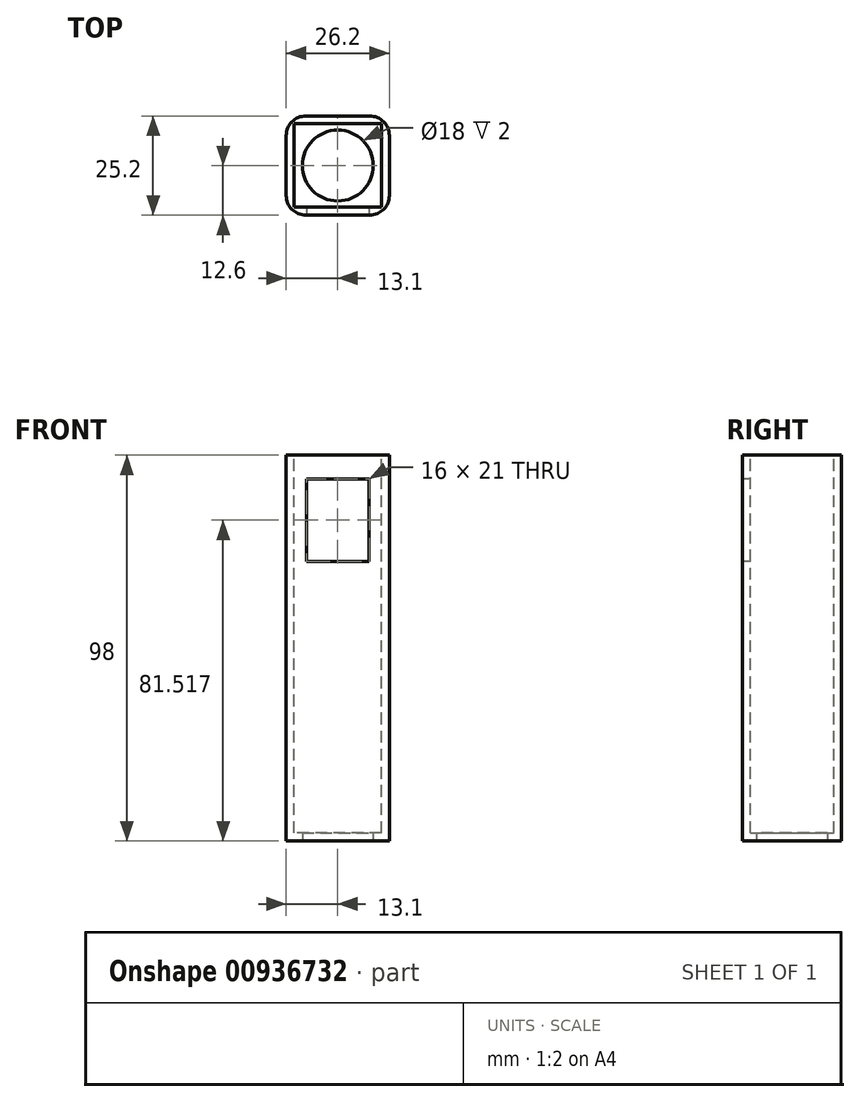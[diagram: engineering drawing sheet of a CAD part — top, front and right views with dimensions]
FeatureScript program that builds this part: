
annotation { "Feature Type Name" : "Feature", "Feature Type Description" : "" }
export const myFeature = defineFeature(function(context is Context, id is Id, definition is map)
    precondition{}
    {
        {
            var Q0;
            Q0=qCreatedBy(makeId("Top.planeOp"),FACE);
            var sketch = newSketch(context, id + "F0", { "sketchPlane" : qUnion([Q0])});
            skLineSegment(sketch, "E0.bottom", {"start": v(13.1, -12.6) * mm, "end": v(-13.1, -12.6) * mm});
            skLineSegment(sketch, "E0.top", {"start": v(13.1, 12.6) * mm, "end": v(-13.1, 12.6) * mm});
            skLineSegment(sketch, "E0.left", {"start": v(13.1, -12.6) * mm, "end": v(13.1, 12.6) * mm});
            skLineSegment(sketch, "E0.right", {"start": v(-13.1, -12.6) * mm, "end": v(-13.1, 12.6) * mm});
            skPoint(sketch, "E0.middle", {"position": v(0, 0) * mm});
            skSolve(sketch);
        }
        {
            var Q0;
            Q0=makeQuery(id+"F0.imprint","IMPRINT",FACE,{"disambiguationData":[TD([[makeQuery(id+"F0.imprint","IMPRINT",EDGE,{"derivedFrom":sQuery(id+"F0.wireOp",EDGE,"E0.bottom")}),-1.0]])]});
            extrude(context, id + "F1", {"entities" : qUnion([Q0]), "oppositeDirection" : true, "depth" : 98 * mm, "offsetDistance" : 25 * mm});
        }
        {
            var Q0;
            Q0=makeQuery(id+"F1.opExtrude","CAP_FACE",FACE,{"disambiguationData":[OSD([sQuery(id+"F0.wireOp",EDGE,"E0.bottom"),sQuery(id+"F0.wireOp",EDGE,"E0.top"),sQuery(id+"F0.wireOp",EDGE,"E0.left"),sQuery(id+"F0.wireOp",EDGE,"E0.right")])],"isStart":true});
            shell(context, id + "F2", {"entities" : qUnion([Q0]), "thickness" : 2 * mm});
        }
        {
            var Q0;
            Q0=makeQuery(id+"F1.opExtrude","CAP_FACE",FACE,{"disambiguationData":[OSD([sQuery(id+"F0.wireOp",EDGE,"E0.bottom"),sQuery(id+"F0.wireOp",EDGE,"E0.top"),sQuery(id+"F0.wireOp",EDGE,"E0.left"),sQuery(id+"F0.wireOp",EDGE,"E0.right")])],"isStart":false});
            var sketch = newSketch(context, id + "F3", { "sketchPlane" : qUnion([Q0])});
            skCircle(sketch, "E1", {"center": v(0, 0) * mm, "radius": 9 * mm});
            skSolve(sketch);
        }
        {
            var Q0;
            Q0=makeQuery(id+"F3.imprint","IMPRINT",FACE,{"disambiguationData":[TD([[makeQuery(id+"F3.imprint","IMPRINT",EDGE,{"derivedFrom":sQuery(id+"F3.wireOp",EDGE,"E1")}),1.0]])]});
            extrude(context, id + "F4", {"entities" : qUnion([Q0]), "operationType" : NewBodyOperationType.REMOVE, "oppositeDirection" : true, "depth" : 2 * mm, "offsetDistance" : 25 * mm});
        }
        {
            var Q0;
            Q0=makeQuery(id+"F1.opExtrude","SWEPT_FACE",FACE,{"disambiguationData":[OSD([sQuery(id+"F0.wireOp",EDGE,"E0.bottom")])]});
            var sketch = newSketch(context, id + "F5", { "sketchPlane" : qUnion([Q0])});
            skLineSegment(sketch, "E2", {"start": v(0, 0) * mm, "end": v(0, -6) * mm});
            skSolve(sketch);
        }
        {
            var Q0;
            {var subQ0=sQuery(id+"F0.wireOp",EDGE,"E0.bottom");Q0=makeQuery(id+"F5.imprint","IMPRINT",FACE,{"disambiguationData":[TD([[makeQuery(id+"F5.imprint","IMPRINT",EDGE,{"derivedFrom":makeQuery(id+"F1.opExtrude","CAP_EDGE",EDGE,{"disambiguationData":[OSD([subQ0])],"isStart":false})}),-1.0]])]});}
            var sketch = newSketch(context, id + "F6", { "sketchPlane" : qUnion([Q0])});
            skLineSegment(sketch, "E3.bottom", {"start": v(8, -26.98) * mm, "end": v(-8, -26.98) * mm});
            skLineSegment(sketch, "E3.top", {"start": v(8, -5.98) * mm, "end": v(-8, -5.98) * mm});
            skLineSegment(sketch, "E3.left", {"start": v(8, -26.98) * mm, "end": v(8, -5.98) * mm});
            skLineSegment(sketch, "E3.right", {"start": v(-8, -26.98) * mm, "end": v(-8, -5.98) * mm});
            skPoint(sketch, "E3.middle", {"position": v(0, -16.48) * mm});
            skSolve(sketch);
        }
        {
            var Q0;
            Q0=makeQuery(id+"F6.imprint","IMPRINT",FACE,{"disambiguationData":[TD([[makeQuery(id+"F6.imprint","IMPRINT",EDGE,{"derivedFrom":sQuery(id+"F6.wireOp",EDGE,"E3.bottom")}),-1.0]])]});
            extrude(context, id + "F7", {"entities" : qUnion([Q0]), "operationType" : NewBodyOperationType.REMOVE, "oppositeDirection" : true, "depth" : 2 * mm, "offsetDistance" : 25 * mm});
        }
        {
            var Q0;
            Q0=makeQuery(id+"F1.opExtrude","SWEPT_EDGE",EDGE,{"disambiguationData":[OSD([sQuery(id+"F0.wireOp",EDGE,"E0.bottom"),sQuery(id+"F0.wireOp",EDGE,"E0.left")])]});
            var Q1;
            Q1=makeQuery(id+"F1.opExtrude","SWEPT_EDGE",EDGE,{"disambiguationData":[OSD([sQuery(id+"F0.wireOp",EDGE,"E0.bottom"),sQuery(id+"F0.wireOp",EDGE,"E0.right")])]});
            var Q2;
            Q2=makeQuery(id+"F1.opExtrude","SWEPT_EDGE",EDGE,{"disambiguationData":[OSD([sQuery(id+"F0.wireOp",EDGE,"E0.top"),sQuery(id+"F0.wireOp",EDGE,"E0.right")])]});
            var Q3;
            Q3=makeQuery(id+"F1.opExtrude","SWEPT_EDGE",EDGE,{"disambiguationData":[OSD([sQuery(id+"F0.wireOp",EDGE,"E0.top"),sQuery(id+"F0.wireOp",EDGE,"E0.left")])]});
            fillet(context, id + "F8", {"entities" : qUnion([Q0, Q1, Q2, Q3]), "radius" : 5 * mm, "tangentPropagation" : true, "allowEdgeOverflow" : false});
        }
    });
